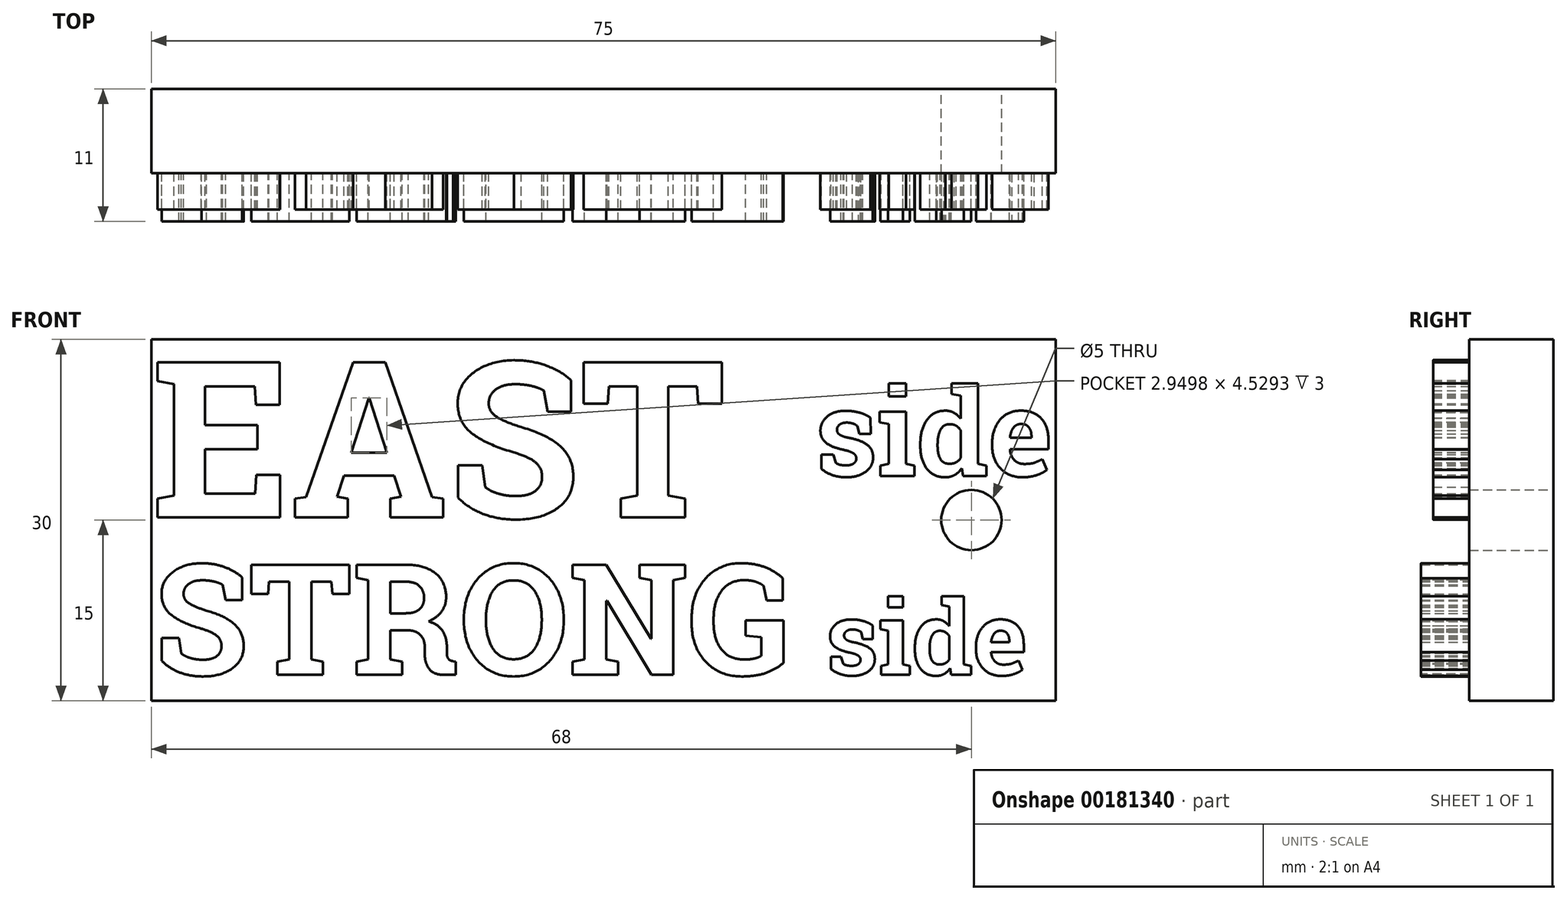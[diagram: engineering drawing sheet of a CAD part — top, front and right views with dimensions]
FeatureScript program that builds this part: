
annotation { "Feature Type Name" : "Feature", "Feature Type Description" : "" }
export const myFeature = defineFeature(function(context is Context, id is Id, definition is map)
    precondition{}
    {
        {
            var Q0;
            Q0=qCreatedBy(makeId("Front.planeOp"),FACE);
            var sketch = newSketch(context, id + "F0", { "sketchPlane" : qUnion([Q0])});
            skLineSegment(sketch, "E0.bottom", {"start": v(0, 0) * mm, "end": v(75, 0) * mm});
            skLineSegment(sketch, "E0.top", {"start": v(0, -30) * mm, "end": v(75, -30) * mm});
            skLineSegment(sketch, "E0.left", {"start": v(0, 0) * mm, "end": v(0, -30) * mm});
            skLineSegment(sketch, "E0.right", {"start": v(75, 0) * mm, "end": v(75, -30) * mm});
            skCircle(sketch, "E1", {"center": v(68, -15) * mm, "radius": 2.5 * mm});
            skSolve(sketch);
        }
        {
            var Q0;
            Q0=makeQuery(id+"F0.imprint","IMPRINT",FACE,{"disambiguationData":[TD([[makeQuery(id+"F0.imprint","IMPRINT",EDGE,{"derivedFrom":sQuery(id+"F0.wireOp",EDGE,"E0.bottom")}),-1.0]])]});
            extrude(context, id + "F1", {"entities" : qUnion([Q0]), "depth" : 7 * mm});
        }
        {
            var Q0;
            Q0=makeQuery(id+"F1.opExtrude","CAP_FACE",FACE,{"disambiguationData":[OSD([sQuery(id+"F0.wireOp",EDGE,"E0.bottom"),sQuery(id+"F0.wireOp",EDGE,"E0.top"),sQuery(id+"F0.wireOp",EDGE,"E0.left"),sQuery(id+"F0.wireOp",EDGE,"E0.right"),sQuery(id+"F0.wireOp",EDGE,"E1")])],"isStart":false});
            var sketch = newSketch(context, id + "F2", { "sketchPlane" : qUnion([Q0])});
            skText(sketch, "E2", { "text": "EAST", "fontName": "RobotoSlab-Bold.ttf"});
            skText(sketch, "E3", { "text": "side", "fontName": "RobotoSlab-Bold.ttf"});
            const initialGuessF2  = {"E2": [0, -0.01478, 1, 0, 0.01302], "E3": [0.055, -0.01135, 1, 0, 0.00725]};
            skSetInitialGuess(sketch, initialGuessF2);
            skSolve(sketch);
        }
        {
            var Q0;
            Q0 = qSketchRegion(id + "F2", true);
            extrude(context, id + "F3", {"entities" : qUnion([Q0]), "operationType" : NewBodyOperationType.ADD, "depth" : 3 * mm});
        }
        {
            var Q0;
            {var subQ0=sQuery(id+"F0.wireOp",EDGE,"E0.left");var subQ1=sQuery(id+"F0.wireOp",EDGE,"E0.bottom");var subQ2=sQuery(id+"F0.wireOp",EDGE,"E0.right");var subQ3=sQuery(id+"F0.wireOp",EDGE,"E0.top");var subQ4=sQuery(id+"F0.wireOp",EDGE,"E1");Q0=makeQuery(id+"F3.boolean.opBoolean","SPLIT",FACE,{"disambiguationData":[TD([makeQuery(id+"F1.opExtrude","SWEPT_FACE",FACE,{"disambiguationData":[OSD([subQ1])]})])],"derivedFrom":makeQuery(id+"F1.opExtrude","CAP_FACE",FACE,{"disambiguationData":[OSD([subQ1,subQ3,subQ0,subQ2,subQ4])],"isStart":false})});}
            var sketch = newSketch(context, id + "F4", { "sketchPlane" : qUnion([Q0])});
            skText(sketch, "E4", { "text": "STRONG", "fontName": "RobotoSlab-Bold.ttf"});
            const initialGuessF4  = {"E4": [0.00023, -0.02784, 1, 0, 0.00925]};
            skSetInitialGuess(sketch, initialGuessF4);
            skSolve(sketch);
        }
        {
            var Q0;
            Q0 = qSketchRegion(id + "F4", true);
            var Q1;
            Q1 = qSketchRegion(id + "F3vl2oHQ9K1xAHF_1", true);
            extrude(context, id + "F5", {"entities" : qUnion([Q0, Q1]), "operationType" : NewBodyOperationType.ADD, "depth" : 4 * mm});
        }
        {
            var Q0;
            {var subQ0=sQuery(id+"F0.wireOp",EDGE,"E1");var subQ102=sQuery(id+"F0.wireOp",EDGE,"E0.top");var subQ105=sQuery(id+"F0.wireOp",EDGE,"E0.right");var subQ113=sQuery(id+"F0.wireOp",EDGE,"E0.bottom");var subQ114=makeQuery(id+"F1.opExtrude","SWEPT_FACE",FACE,{"disambiguationData":[OSD([subQ113])]});var subQ147=sQuery(id+"F0.wireOp",EDGE,"E0.left");Q0=makeQuery(id+"F5.boolean.opBoolean","SPLIT",FACE,{"disambiguationData":[TD([subQ114])],"derivedFrom":makeQuery(id+"F3.boolean.opBoolean","SPLIT",FACE,{"disambiguationData":[TD([subQ114])],"derivedFrom":makeQuery(id+"F1.opExtrude","CAP_FACE",FACE,{"disambiguationData":[OSD([subQ113,subQ102,subQ147,subQ105,subQ0])],"isStart":false})})});}
            var sketch = newSketch(context, id + "F6", { "sketchPlane" : qUnion([Q0])});
            skText(sketch, "E5", { "text": "side", "fontName": "RobotoSlab-Bold.ttf"});
            const initialGuessF6  = {"E5": [0.05587, -0.02784, 1, 0, 0.00616]};
            skSetInitialGuess(sketch, initialGuessF6);
            skSolve(sketch);
        }
        {
            var Q0;
            Q0 = qSketchRegion(id + "F6", true);
            extrude(context, id + "F7", {"entities" : qUnion([Q0]), "operationType" : NewBodyOperationType.ADD, "depth" : 4 * mm});
        }
    });
